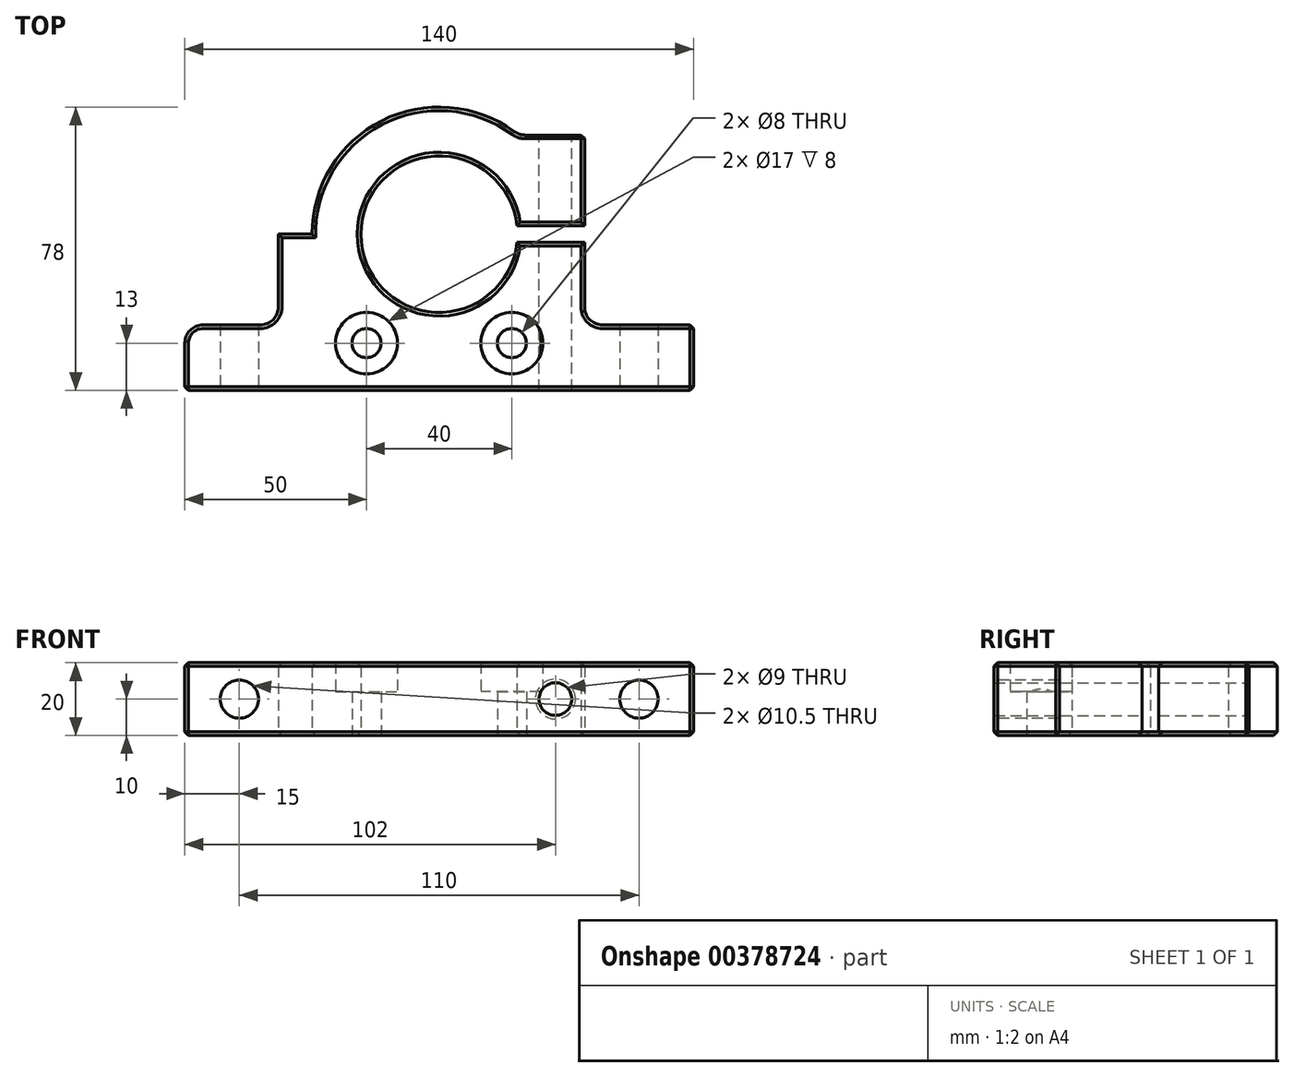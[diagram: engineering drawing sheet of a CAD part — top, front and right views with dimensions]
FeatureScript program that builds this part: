
annotation { "Feature Type Name" : "Feature", "Feature Type Description" : "" }
export const myFeature = defineFeature(function(context is Context, id is Id, definition is map)
    precondition{}
    {
        {
            var Q0;
            Q0=qCreatedBy(makeId("Top.planeOp"),FACE);
            var sketch = newSketch(context, id + "F0", { "sketchPlane" : qUnion([Q0])});
            skArc(sketch, "E0", {"start": v(21.43, 2.3) * mm, "mid": v(-21.55, 0) * mm, "end": v(21.43, -2.3) * mm});
            skArc(sketch, "E1", {"start": v(21.93, 27.28) * mm, "mid": v(-32.04, -14.08) * mm, "end": v(34.92, -2.3) * mm});
            skLineSegment(sketch, "E2", {"start": v(21.43, 2.3) * mm, "end": v(40, 2.3) * mm});
            skLineSegment(sketch, "E3", {"start": v(21.43, -2.3) * mm, "end": v(34.92, -2.3) * mm});
            skLineSegment(sketch, "E4", {"start": v(40, -2.3) * mm, "end": v(40, -25) * mm});
            skLineSegment(sketch, "E5", {"start": v(40, -25) * mm, "end": v(70, -25) * mm});
            skLineSegment(sketch, "E6", {"start": v(70, -25) * mm, "end": v(70, -43) * mm});
            skLineSegment(sketch, "E7", {"start": v(70, -43) * mm, "end": v(-70, -43) * mm});
            skLineSegment(sketch, "E8", {"start": v(-70, -43) * mm, "end": v(-70, -25) * mm});
            skLineSegment(sketch, "E9", {"start": v(-70, -25) * mm, "end": v(-35, -25) * mm});
            skLineSegment(sketch, "E10", {"start": v(-35, -25) * mm, "end": v(-35, 0) * mm});
            skLineSegment(sketch, "E11", {"start": v(40, 2.3) * mm, "end": v(40, 27.28) * mm});
            skLineSegment(sketch, "E12", {"start": v(40, 27.28) * mm, "end": v(21.93, 27.28) * mm});
            skLineSegment(sketch, "E13", {"start": v(34.92, -2.3) * mm, "end": v(40, -2.3) * mm});
            skLineSegment(sketch, "E14", {"start": v(-35, 0) * mm, "end": v(-44.25, 0) * mm});
            skLineSegment(sketch, "E15", {"start": v(-44.25, 0) * mm, "end": v(-44.25, -25) * mm});
            skSolve(sketch);
        }
        {
            var Q0;
            Q0 = qSketchRegion(id + "F0", true);
            extrude(context, id + "F1", {"entities" : qUnion([Q0]), "depth" : 20 * mm});
        }
        {
            var Q0;
            Q0=makeQuery(id+"F1.opExtrude","SWEPT_FACE",FACE,{"disambiguationData":[OSD([sQuery(id+"F0.wireOp",EDGE,"E3")])]});
            var sketch = newSketch(context, id + "F2", { "sketchPlane" : qUnion([Q0])});
            skPoint(sketch, "E16", {"position": v(-32, 10) * mm});
            skSolve(sketch);
        }
        {
            var Q0;
            Q0=sQuery(id+"F2.wireOp",VERTEX,"E16");
            var Q1;
            Q1=sQuery(id+"F2.wireOp",VERTEX,"18bb9694-b6f7-4073-8a90-d65dc3a34b4a");
            var Q2;
            Q2=makeQuery(id+"F1.opExtrude","SWEPT_BODY",BODY,{"disambiguationData":[OSD([sQuery(id+"F0.wireOp",EDGE,"E0"),sQuery(id+"F0.wireOp",EDGE,"E1"),sQuery(id+"F0.wireOp",EDGE,"E2"),sQuery(id+"F0.wireOp",EDGE,"E3")])]});
            hole(context, id + "F3", {"style" : HoleStyle.SIMPLE, "endStyle" : HoleEndStyle.THROUGH, "standardTappedOrClearance" : lookupTablePath({ "standard" : "ISO", "fit" : "Normal", "size" : "M8", "type" : "Clearance" }), "standardBlindInLast" : lookupTablePath({ "fit" : "Standard", "standard" : "ISO", "size" : "M8", "type" : "Clearance" }), "holeDiameter" : 8.8 * mm, "isTappedThrough" : true, "tappedDepth" : 12 * mm, "tapClearance" : 3, "locations" : qUnion([Q0, Q1]), "scope" : qUnion([Q2]), "startStyle" : HoleStartStyle.PART});
        }
        {
            var Q0;
            Q0=sQuery(id+"F2.wireOp",VERTEX,"E16");
            var Q1;
            Q1=sQuery(id+"F2.wireOp",VERTEX,"18bb9694-b6f7-4073-8a90-d65dc3a34b4a");
            var Q2;
            Q2=makeQuery(id+"F1.opExtrude","SWEPT_BODY",BODY,{"disambiguationData":[OSD([sQuery(id+"F0.wireOp",EDGE,"E0"),sQuery(id+"F0.wireOp",EDGE,"E1"),sQuery(id+"F0.wireOp",EDGE,"E2"),sQuery(id+"F0.wireOp",EDGE,"E3")])]});
            hole(context, id + "F4", {"style" : HoleStyle.SIMPLE, "endStyle" : HoleEndStyle.THROUGH, "oppositeDirection" : true, "holeDiameter" : 9 * mm, "isTappedThrough" : true, "tappedDepth" : 12 * mm, "tapClearance" : 3, "locations" : qUnion([Q0, Q1]), "scope" : qUnion([Q2]), "startStyle" : HoleStartStyle.PART});
        }
        {
            var Q0;
            Q0=makeQuery(id+"F1.opExtrude","SWEPT_FACE",FACE,{"disambiguationData":[OSD([sQuery(id+"F0.wireOp",EDGE,"E9")])]});
            var sketch = newSketch(context, id + "F5", { "sketchPlane" : qUnion([Q0])});
            skPoint(sketch, "E17", {"position": v(-55, 10) * mm});
            skPoint(sketch, "E18", {"position": v(55, 10) * mm});
            skSolve(sketch);
        }
        {
            var Q0;
            Q0=sQuery(id+"F5.wireOp",VERTEX,"E18");
            var Q1;
            Q1=sQuery(id+"F5.wireOp",VERTEX,"E17");
            var Q2;
            Q2=makeQuery(id+"F1.opExtrude","SWEPT_BODY",BODY,{"disambiguationData":[OSD([sQuery(id+"F0.wireOp",EDGE,"E0"),sQuery(id+"F0.wireOp",EDGE,"E1"),sQuery(id+"F0.wireOp",EDGE,"E2"),sQuery(id+"F0.wireOp",EDGE,"E3"),sQuery(id+"F0.wireOp",EDGE,"E4"),sQuery(id+"F0.wireOp",EDGE,"E5"),sQuery(id+"F0.wireOp",EDGE,"E6"),sQuery(id+"F0.wireOp",EDGE,"E7"),sQuery(id+"F0.wireOp",EDGE,"E8"),sQuery(id+"F0.wireOp",EDGE,"E9"),sQuery(id+"F0.wireOp",EDGE,"E10")])]});
            hole(context, id + "F6", {"style" : HoleStyle.SIMPLE, "endStyle" : HoleEndStyle.THROUGH, "holeDiameter" : 10.5 * mm, "isTappedThrough" : true, "tappedDepth" : 12 * mm, "tapClearance" : 3, "locations" : qUnion([Q0, Q1]), "scope" : qUnion([Q2]), "startStyle" : HoleStartStyle.PART});
        }
        {
            var Q0;
            Q0=makeQuery(id+"F1.opExtrude","SWEPT_EDGE",EDGE,{"disambiguationData":[OSD([sQuery(id+"F0.wireOp",EDGE,"E4"),sQuery(id+"F0.wireOp",EDGE,"E5")])]});
            var Q1;
            Q1=makeQuery(id+"F1.opExtrude","SWEPT_EDGE",EDGE,{"disambiguationData":[OSD([sQuery(id+"F0.wireOp",EDGE,"E1"),sQuery(id+"F0.wireOp",EDGE,"E12")])]});
            var Q2;
            Q2=makeQuery(id+"F1.opExtrude","SWEPT_EDGE",EDGE,{"disambiguationData":[OSD([sQuery(id+"F0.wireOp",EDGE,"E9"),sQuery(id+"F0.wireOp",EDGE,"E10")])]});
            fillet(context, id + "F7", {"entities" : qUnion([Q0, Q1, Q2]), "radius" : 5 * mm, "tangentPropagation" : true, "allowEdgeOverflow" : false});
        }
        {
            var Q0;
            Q0=makeQuery(id+"F1.opExtrude","CAP_FACE",FACE,{"disambiguationData":[OSD([sQuery(id+"F0.wireOp",EDGE,"E0"),sQuery(id+"F0.wireOp",EDGE,"E1"),sQuery(id+"F0.wireOp",EDGE,"E2"),sQuery(id+"F0.wireOp",EDGE,"E3"),sQuery(id+"F0.wireOp",EDGE,"E4"),sQuery(id+"F0.wireOp",EDGE,"E5"),sQuery(id+"F0.wireOp",EDGE,"E6"),sQuery(id+"F0.wireOp",EDGE,"E7"),sQuery(id+"F0.wireOp",EDGE,"E8"),sQuery(id+"F0.wireOp",EDGE,"E9"),sQuery(id+"F0.wireOp",EDGE,"E10"),sQuery(id+"F0.wireOp",EDGE,"E11"),sQuery(id+"F0.wireOp",EDGE,"E12")])],"isStart":false});
            var Q1;
            Q1=makeQuery(id+"F1.opExtrude","CAP_FACE",FACE,{"disambiguationData":[OSD([sQuery(id+"F0.wireOp",EDGE,"E0"),sQuery(id+"F0.wireOp",EDGE,"E1"),sQuery(id+"F0.wireOp",EDGE,"E2"),sQuery(id+"F0.wireOp",EDGE,"E3"),sQuery(id+"F0.wireOp",EDGE,"E4"),sQuery(id+"F0.wireOp",EDGE,"E5"),sQuery(id+"F0.wireOp",EDGE,"E6"),sQuery(id+"F0.wireOp",EDGE,"E7"),sQuery(id+"F0.wireOp",EDGE,"E8"),sQuery(id+"F0.wireOp",EDGE,"E9"),sQuery(id+"F0.wireOp",EDGE,"E10"),sQuery(id+"F0.wireOp",EDGE,"E11"),sQuery(id+"F0.wireOp",EDGE,"E12")])],"isStart":true});
            var Q2;
            Q2=makeQuery(id+"F1.opExtrude","SWEPT_FACE",FACE,{"disambiguationData":[OSD([sQuery(id+"F0.wireOp",EDGE,"E12")])]});
            var Q3;
            Q3=makeQuery(id+"F1.opExtrude","SWEPT_FACE",FACE,{"disambiguationData":[OSD([sQuery(id+"F0.wireOp",EDGE,"E8")])]});
            var Q4;
            Q4=makeQuery(id+"F1.opExtrude","SWEPT_FACE",FACE,{"disambiguationData":[OSD([sQuery(id+"F0.wireOp",EDGE,"E6")])]});
            chamfer(context, id + "F8", {"entities" : qUnion([Q0, Q1, Q2, Q3, Q4]), "width" : 1 * mm, "tangentPropagation" : true});
        }
        {
            var Q0;
            Q0=makeQuery(id+"F1.opExtrude","CAP_FACE",FACE,{"disambiguationData":[OSD([sQuery(id+"F0.wireOp",EDGE,"E0"),sQuery(id+"F0.wireOp",EDGE,"E1"),sQuery(id+"F0.wireOp",EDGE,"E2"),sQuery(id+"F0.wireOp",EDGE,"E3"),sQuery(id+"F0.wireOp",EDGE,"E4"),sQuery(id+"F0.wireOp",EDGE,"E5"),sQuery(id+"F0.wireOp",EDGE,"E6"),sQuery(id+"F0.wireOp",EDGE,"E7"),sQuery(id+"F0.wireOp",EDGE,"E8"),sQuery(id+"F0.wireOp",EDGE,"E9"),sQuery(id+"F0.wireOp",EDGE,"E10"),sQuery(id+"F0.wireOp",EDGE,"E11"),sQuery(id+"F0.wireOp",EDGE,"E12"),sQuery(id+"F0.wireOp",EDGE,"E13")])],"isStart":false});
            var sketch = newSketch(context, id + "F9", { "sketchPlane" : qUnion([Q0]), "disableImprinting" : false});
            skPoint(sketch, "E19", {"position": v(-20, -30) * mm});
            skPoint(sketch, "E20.MirrorP", {"position": v(20, -30) * mm});
            skSolve(sketch);
        }
        {
            var Q0;
            Q0=sQuery(id+"F9.wireOp",VERTEX,"E19");
            var Q1;
            Q1=sQuery(id+"F9.wireOp",VERTEX,"E20.MirrorP");
            var Q2;
            Q2=makeQuery(id+"F1.opExtrude","SWEPT_BODY",BODY,{"disambiguationData":[OSD([sQuery(id+"F0.wireOp",EDGE,"E0"),sQuery(id+"F0.wireOp",EDGE,"E1"),sQuery(id+"F0.wireOp",EDGE,"E2"),sQuery(id+"F0.wireOp",EDGE,"E3"),sQuery(id+"F0.wireOp",EDGE,"E4"),sQuery(id+"F0.wireOp",EDGE,"E5"),sQuery(id+"F0.wireOp",EDGE,"E6"),sQuery(id+"F0.wireOp",EDGE,"E7"),sQuery(id+"F0.wireOp",EDGE,"E8"),sQuery(id+"F0.wireOp",EDGE,"E9"),sQuery(id+"F0.wireOp",EDGE,"E10"),sQuery(id+"F0.wireOp",EDGE,"E11"),sQuery(id+"F0.wireOp",EDGE,"E12"),sQuery(id+"F0.wireOp",EDGE,"E13")])]});
            hole(context, id + "F10", {"style" : HoleStyle.C_BORE, "endStyle" : HoleEndStyle.THROUGH, "holeDiameter" : 8 * mm, "cBoreDiameter" : 17 * mm, "cBoreDepth" : 8 * mm, "isTappedThrough" : true, "tappedDepth" : 12 * mm, "tapClearance" : 3, "locations" : qUnion([Q0, Q1]), "scope" : qUnion([Q2]), "startStyle" : HoleStartStyle.PART});
        }
    });
